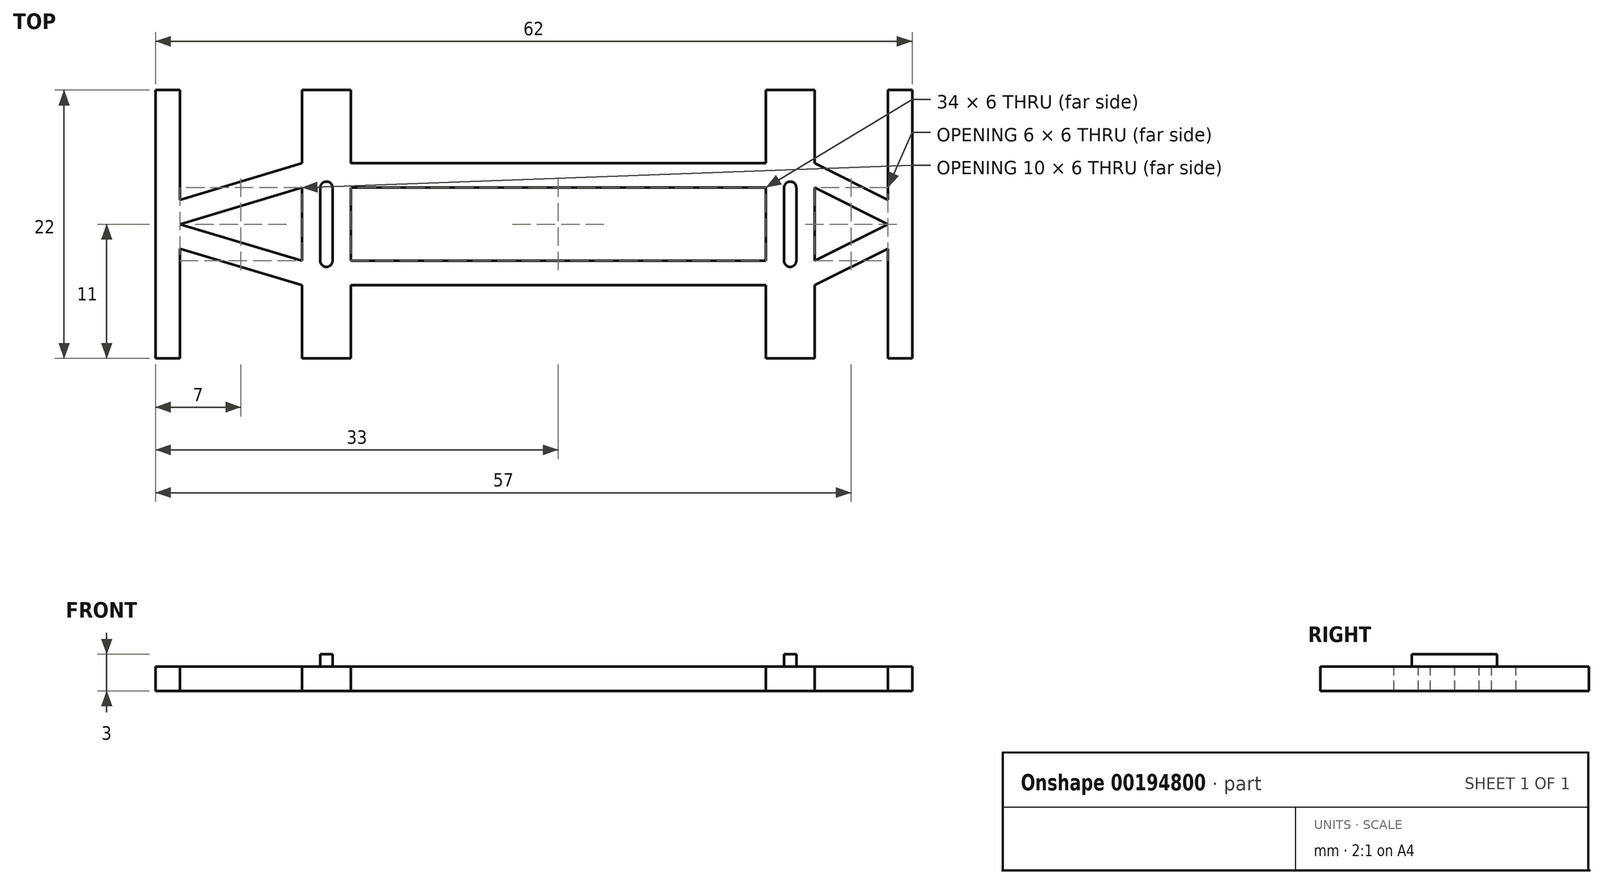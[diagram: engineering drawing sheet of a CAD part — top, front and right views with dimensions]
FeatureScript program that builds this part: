
annotation { "Feature Type Name" : "Feature", "Feature Type Description" : "" }
export const myFeature = defineFeature(function(context is Context, id is Id, definition is map)
    precondition{}
    {
        {
            var Q0;
            Q0=qCreatedBy(makeId("Top.planeOp"),FACE);
            var sketch = newSketch(context, id + "F0", { "sketchPlane" : qUnion([Q0])});
            skLineSegment(sketch, "E0", {"start": v(-43.98, 11) * mm, "end": v(82.07, 11) * mm, "construction": true});
            skLineSegment(sketch, "E1", {"start": v(0, 11) * mm, "end": v(0, 0) * mm});
            skLineSegment(sketch, "E2", {"start": v(0, 0) * mm, "end": v(2, 0) * mm});
            skLineSegment(sketch, "E3", {"start": v(2, 0) * mm, "end": v(2, 9) * mm});
            skLineSegment(sketch, "E4", {"start": v(2, 9) * mm, "end": v(12, 6) * mm});
            skLineSegment(sketch, "E5", {"start": v(12, 6) * mm, "end": v(12, 0) * mm});
            skLineSegment(sketch, "E6", {"start": v(12, 0) * mm, "end": v(16, 0) * mm});
            skLineSegment(sketch, "E7", {"start": v(16, 0) * mm, "end": v(16, 6) * mm});
            skLineSegment(sketch, "E8", {"start": v(16, 6) * mm, "end": v(50, 6) * mm});
            skLineSegment(sketch, "E9", {"start": v(50, 6) * mm, "end": v(50, 0) * mm});
            skLineSegment(sketch, "E10", {"start": v(50, 0) * mm, "end": v(54, 0) * mm});
            skLineSegment(sketch, "E11", {"start": v(54, 0) * mm, "end": v(54, 6) * mm});
            skLineSegment(sketch, "E12", {"start": v(54, 6) * mm, "end": v(60, 9) * mm});
            skLineSegment(sketch, "E13", {"start": v(60, 9) * mm, "end": v(60, 0) * mm});
            skLineSegment(sketch, "E14", {"start": v(60, 0) * mm, "end": v(62, 0) * mm});
            skLineSegment(sketch, "E15", {"start": v(62, 0) * mm, "end": v(62, 11) * mm});
            skLineSegment(sketch, "E16", {"start": v(2, 11) * mm, "end": v(12, 8) * mm});
            skLineSegment(sketch, "E17", {"start": v(12, 8) * mm, "end": v(12, 11) * mm});
            skLineSegment(sketch, "E18", {"start": v(16, 8) * mm, "end": v(50, 8) * mm});
            skLineSegment(sketch, "E19", {"start": v(50, 8) * mm, "end": v(50, 11) * mm});
            skLineSegment(sketch, "E20", {"start": v(16, 8) * mm, "end": v(16, 11) * mm});
            skLineSegment(sketch, "E21", {"start": v(54, 8) * mm, "end": v(60, 11) * mm});
            skLineSegment(sketch, "E22", {"start": v(54, 8) * mm, "end": v(54, 11) * mm});
            skLineSegment(sketch, "E23.MirrorCS", {"start": v(60, 22) * mm, "end": v(62, 22) * mm});
            skLineSegment(sketch, "E24.MirrorCS", {"start": v(0, 22) * mm, "end": v(2, 22) * mm});
            skLineSegment(sketch, "E25.MirrorCS", {"start": v(12, 22) * mm, "end": v(16, 22) * mm});
            skLineSegment(sketch, "E26.MirrorCS", {"start": v(2, 11) * mm, "end": v(12, 14) * mm});
            skLineSegment(sketch, "E27.MirrorCS", {"start": v(12, 16) * mm, "end": v(12, 22) * mm});
            skLineSegment(sketch, "E28.MirrorCS", {"start": v(16, 16) * mm, "end": v(50, 16) * mm});
            skLineSegment(sketch, "E29.MirrorCS", {"start": v(50, 16) * mm, "end": v(50, 22) * mm});
            skLineSegment(sketch, "E30.MirrorCS", {"start": v(62, 22) * mm, "end": v(62, 11) * mm});
            skLineSegment(sketch, "E31.MirrorCS", {"start": v(12, 14) * mm, "end": v(12, 11) * mm});
            skLineSegment(sketch, "E32.MirrorCS", {"start": v(50, 22) * mm, "end": v(54, 22) * mm});
            skLineSegment(sketch, "E33.MirrorCS", {"start": v(60, 13) * mm, "end": v(60, 22) * mm});
            skLineSegment(sketch, "E34.MirrorCS", {"start": v(54, 22) * mm, "end": v(54, 16) * mm});
            skLineSegment(sketch, "E35.MirrorCS", {"start": v(54, 16) * mm, "end": v(60, 13) * mm});
            skLineSegment(sketch, "E36.MirrorCS", {"start": v(54, 14) * mm, "end": v(54, 11) * mm});
            skLineSegment(sketch, "E37.MirrorCS", {"start": v(2, 13) * mm, "end": v(12, 16) * mm});
            skLineSegment(sketch, "E38.MirrorCS", {"start": v(54, 14) * mm, "end": v(60, 11) * mm});
            skLineSegment(sketch, "E39.MirrorCS", {"start": v(16, 14) * mm, "end": v(50, 14) * mm});
            skLineSegment(sketch, "E40.MirrorCS", {"start": v(50, 14) * mm, "end": v(50, 11) * mm});
            skLineSegment(sketch, "E41.MirrorCS", {"start": v(0, 11) * mm, "end": v(0, 22) * mm});
            skLineSegment(sketch, "E42.MirrorCS", {"start": v(16, 22) * mm, "end": v(16, 16) * mm});
            skLineSegment(sketch, "E43.MirrorCS", {"start": v(16, 14) * mm, "end": v(16, 11) * mm});
            skLineSegment(sketch, "E44.MirrorCS", {"start": v(2, 22) * mm, "end": v(2, 13) * mm});
            skSolve(sketch);
        }
        {
            var Q0;
            Q0 = qSketchRegion(id + "F0", true);
            extrude(context, id + "F1", {"entities" : qUnion([Q0]), "depth" : 2 * mm});
        }
        {
            var Q0;
            Q0=makeQuery(id+"F1.opExtrude","CAP_FACE",FACE,{"disambiguationData":[OSD([sQuery(id+"F0.wireOp",EDGE,"E1"),sQuery(id+"F0.wireOp",EDGE,"E2"),sQuery(id+"F0.wireOp",EDGE,"E3"),sQuery(id+"F0.wireOp",EDGE,"E4"),sQuery(id+"F0.wireOp",EDGE,"E5"),sQuery(id+"F0.wireOp",EDGE,"E6"),sQuery(id+"F0.wireOp",EDGE,"E7"),sQuery(id+"F0.wireOp",EDGE,"E8"),sQuery(id+"F0.wireOp",EDGE,"E9"),sQuery(id+"F0.wireOp",EDGE,"E10"),sQuery(id+"F0.wireOp",EDGE,"E11"),sQuery(id+"F0.wireOp",EDGE,"E12"),sQuery(id+"F0.wireOp",EDGE,"E13"),sQuery(id+"F0.wireOp",EDGE,"E14"),sQuery(id+"F0.wireOp",EDGE,"E15"),sQuery(id+"F0.wireOp",EDGE,"E16"),sQuery(id+"F0.wireOp",EDGE,"E17"),sQuery(id+"F0.wireOp",EDGE,"E18"),sQuery(id+"F0.wireOp",EDGE,"E19"),sQuery(id+"F0.wireOp",EDGE,"E20"),sQuery(id+"F0.wireOp",EDGE,"E21"),sQuery(id+"F0.wireOp",EDGE,"E22"),sQuery(id+"F0.wireOp",EDGE,"E23.MirrorCS"),sQuery(id+"F0.wireOp",EDGE,"E24.MirrorCS"),sQuery(id+"F0.wireOp",EDGE,"E25.MirrorCS"),sQuery(id+"F0.wireOp",EDGE,"E26.MirrorCS"),sQuery(id+"F0.wireOp",EDGE,"E27.MirrorCS"),sQuery(id+"F0.wireOp",EDGE,"E28.MirrorCS"),sQuery(id+"F0.wireOp",EDGE,"E29.MirrorCS"),sQuery(id+"F0.wireOp",EDGE,"E30.MirrorCS"),sQuery(id+"F0.wireOp",EDGE,"E31.MirrorCS"),sQuery(id+"F0.wireOp",EDGE,"E32.MirrorCS"),sQuery(id+"F0.wireOp",EDGE,"E33.MirrorCS"),sQuery(id+"F0.wireOp",EDGE,"E34.MirrorCS"),sQuery(id+"F0.wireOp",EDGE,"E35.MirrorCS"),sQuery(id+"F0.wireOp",EDGE,"E36.MirrorCS"),sQuery(id+"F0.wireOp",EDGE,"E37.MirrorCS"),sQuery(id+"F0.wireOp",EDGE,"E38.MirrorCS"),sQuery(id+"F0.wireOp",EDGE,"E39.MirrorCS"),sQuery(id+"F0.wireOp",EDGE,"E40.MirrorCS"),sQuery(id+"F0.wireOp",EDGE,"E41.MirrorCS"),sQuery(id+"F0.wireOp",EDGE,"E42.MirrorCS"),sQuery(id+"F0.wireOp",EDGE,"E43.MirrorCS"),sQuery(id+"F0.wireOp",EDGE,"E44.MirrorCS")])],"isStart":false});
            var sketch = newSketch(context, id + "F2", { "sketchPlane" : qUnion([Q0])});
            skLineSegment(sketch, "E45", {"start": v(14, 14) * mm, "end": v(14, 8) * mm, "construction": true});
            skArc(sketch, "E46", {"start": v(14.5, 14) * mm, "mid": v(14, 14.5) * mm, "end": v(13.5, 14) * mm});
            skArc(sketch, "E47", {"start": v(14.5, 8) * mm, "mid": v(14, 7.5) * mm, "end": v(13.5, 8) * mm});
            skLineSegment(sketch, "E48", {"start": v(13.5, 14) * mm, "end": v(13.5, 8) * mm});
            skLineSegment(sketch, "E49", {"start": v(14.5, 8) * mm, "end": v(14.5, 14) * mm});
            skLineSegment(sketch, "E50", {"start": v(14, 14) * mm, "end": v(16, 14) * mm, "construction": true});
            skLineSegment(sketch, "E51", {"start": v(14, 8) * mm, "end": v(16, 8) * mm, "construction": true});
            skPoint(sketch, "E52.start.orphan", {"position": v(33, 16) * mm});
            skPoint(sketch, "E53.endSnap0", {"position": v(33, 14) * mm});
            skPoint(sketch, "E54.orphan", {"position": v(33, 8) * mm});
            skPoint(sketch, "E55.start.orphan", {"position": v(33, 6) * mm});
            skLineSegment(sketch, "E56", {"start": v(33, 0) * mm, "end": v(33, 24.9) * mm, "construction": true});
            skArc(sketch, "E57.MirrorCS", {"start": v(51.5, 14) * mm, "mid": v(52, 14.5) * mm, "end": v(52.5, 14) * mm});
            skArc(sketch, "E58.MirrorCS", {"start": v(51.5, 8) * mm, "mid": v(52, 7.5) * mm, "end": v(52.5, 8) * mm});
            skLineSegment(sketch, "E59.MirrorCS", {"start": v(51.5, 8) * mm, "end": v(51.5, 14) * mm});
            skLineSegment(sketch, "E60.MirrorCS", {"start": v(52.5, 14) * mm, "end": v(52.5, 8) * mm});
            skLineSegment(sketch, "E61.MirrorCS", {"start": v(52, 14) * mm, "end": v(52, 8) * mm, "construction": true});
            skLineSegment(sketch, "E62.MirrorCS", {"start": v(52, 8) * mm, "end": v(50, 8) * mm, "construction": true});
            skLineSegment(sketch, "E63.MirrorCS", {"start": v(52, 14) * mm, "end": v(50, 14) * mm, "construction": true});
            skSolve(sketch);
        }
        {
            var Q0;
            Q0 = qSketchRegion(id + "F2", true);
            extrude(context, id + "F3", {"entities" : qUnion([Q0]), "operationType" : NewBodyOperationType.ADD, "depth" : 1 * mm});
        }
    });
